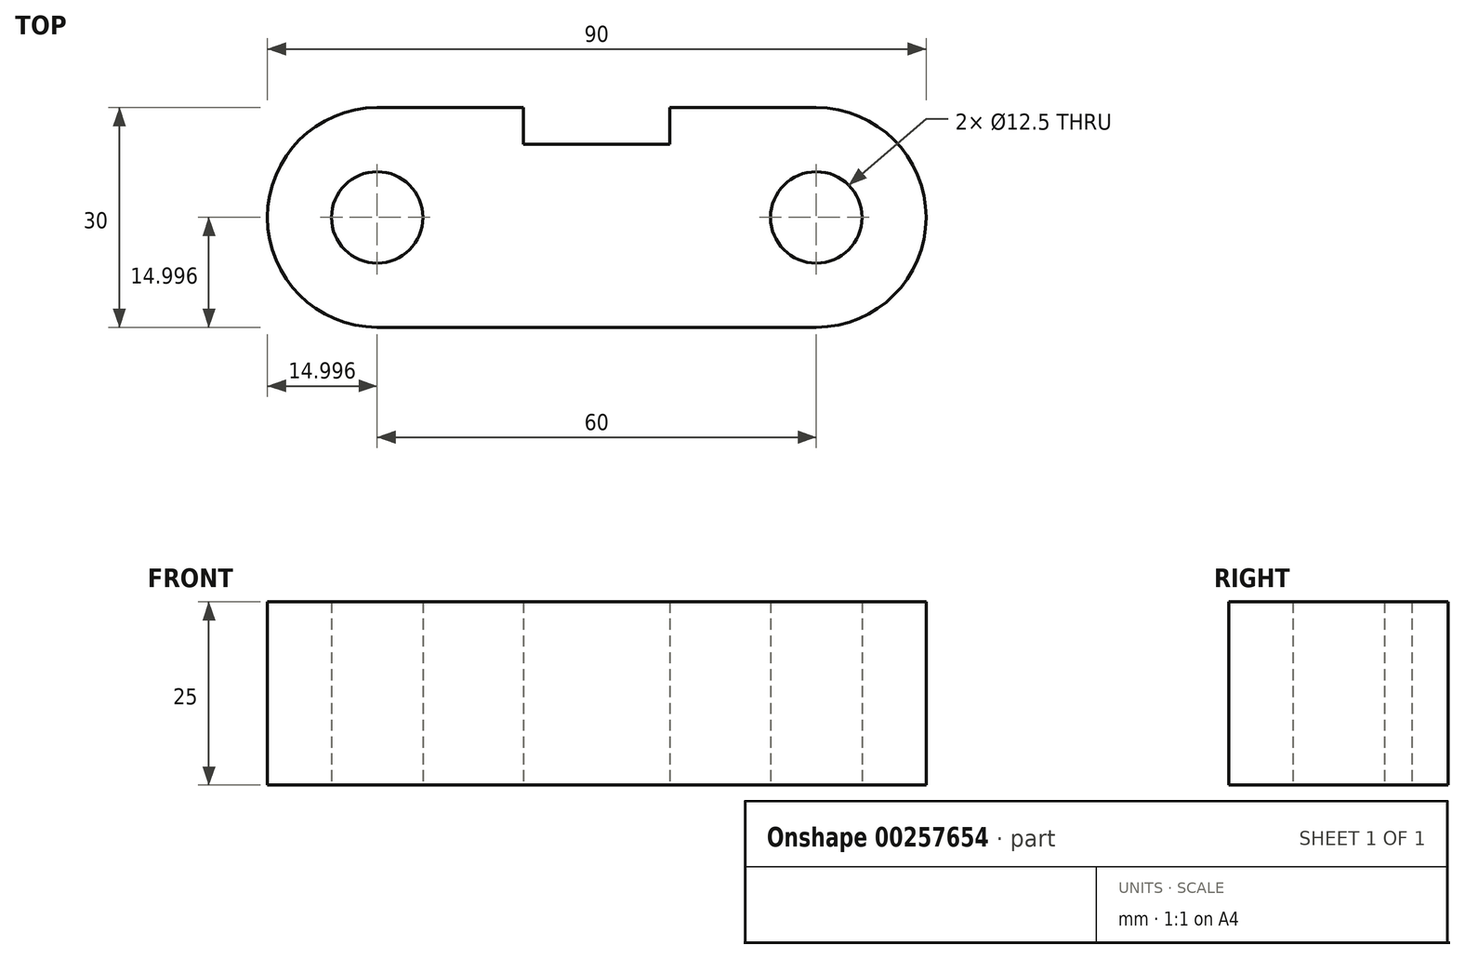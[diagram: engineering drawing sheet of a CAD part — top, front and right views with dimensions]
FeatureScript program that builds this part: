
annotation { "Feature Type Name" : "Feature", "Feature Type Description" : "" }
export const myFeature = defineFeature(function(context is Context, id is Id, definition is map)
    precondition{}
    {
        {
            var Q0;
            Q0=qCreatedBy(makeId("Top.planeOp"),FACE);
            var sketch = newSketch(context, id + "F0", { "sketchPlane" : qUnion([Q0])});
            skLineSegment(sketch, "E0", {"start": v(-35.05, -37.16) * mm, "end": v(24.95, -37.16) * mm});
            skLineSegment(sketch, "E1", {"start": v(39.95, -22.16) * mm, "end": v(39.95, -22.16) * mm});
            skLineSegment(sketch, "E2", {"start": v(-50.05, -22.16) * mm, "end": v(-50.05, -22.16) * mm});
            skPoint(sketch, "E3.visualSharp", {"position": v(-50.05, -7.16) * mm});
            skArc(sketch, "E3.filletArc", {"start": v(-35.05, -7.16) * mm, "mid": v(-45.66, -11.56) * mm, "end": v(-50.05, -22.16) * mm});
            skPoint(sketch, "E4.visualSharp", {"position": v(-50.05, -37.16) * mm});
            skArc(sketch, "E4.filletArc", {"start": v(-50.05, -22.16) * mm, "mid": v(-45.66, -32.77) * mm, "end": v(-35.05, -37.16) * mm});
            skPoint(sketch, "E5.visualSharp", {"position": v(39.95, -37.16) * mm});
            skArc(sketch, "E5.filletArc", {"start": v(24.95, -37.16) * mm, "mid": v(35.55, -32.77) * mm, "end": v(39.95, -22.16) * mm});
            skPoint(sketch, "E6.visualSharp", {"position": v(39.95, -7.16) * mm});
            skArc(sketch, "E6.filletArc", {"start": v(39.95, -22.16) * mm, "mid": v(35.55, -11.56) * mm, "end": v(24.95, -7.16) * mm});
            skLineSegment(sketch, "E7", {"start": v(24.95, -7.16) * mm, "end": v(4.95, -7.16) * mm});
            skLineSegment(sketch, "E8", {"start": v(4.95, -7.16) * mm, "end": v(4.95, -12.16) * mm});
            skLineSegment(sketch, "E9", {"start": v(4.95, -12.16) * mm, "end": v(-15.05, -12.16) * mm});
            skLineSegment(sketch, "E10", {"start": v(-15.05, -12.16) * mm, "end": v(-15.05, -7.16) * mm});
            skLineSegment(sketch, "E11", {"start": v(-15.05, -7.16) * mm, "end": v(-35.05, -7.16) * mm});
            skCircle(sketch, "E12", {"center": v(-35.05, -22.16) * mm, "radius": 6.25 * mm});
            skCircle(sketch, "E13", {"center": v(24.95, -22.16) * mm, "radius": 6.25 * mm});
            skSolve(sketch);
        }
        {
            var Q0;
            Q0=makeQuery(id+"F0.imprint","IMPRINT",FACE,{"disambiguationData":[TD([[makeQuery(id+"F0.imprint","IMPRINT",EDGE,{"derivedFrom":sQuery(id+"F0.wireOp",EDGE,"E0")}),1.0]])]});
            extrude(context, id + "F1", {"entities" : qUnion([Q0]), "depth" : 25 * mm});
        }
    });
